# Revit family: Flush_valve-Manual-Zurn-Exposed-Water_closet-Z6000
name_source: partatom
category: Plumbing Fixtures
units: mm (PartAtom-declared; Revit-internal decimal feet)

## family parameters
Cut with Voids When Loaded = No
Host = Face
Maintain Annotation Orientation = No
OmniClass Number = 23.45.05.14.99
OmniClass Title = Other Sanitary Washing Plumbing Fixtures
Part Type = Normal
Room Calculation Point = No
Round Connector Dimension = Use Radius
Shared = No

## types (24) — shared parameters
Activation Method = Manual Operated
Assembly Code = D2010.60
CW Connection = Yes
Centerline of Stop Valve to Centerline of Flush Valve = 4.75 "
Default Elevation = 48 "
Description = Exposed Flush Valve for Water Closets
HW Connection = No
Inlet Connection Size (inch) = 1 "
Main Material = Chrome-Plated Brass - Zurn - Polished
Manufacturer = Zurn Water, LLC
Manufacturer Brand = Zurn
Max Working Water Temperature = 104 °F
Model = Z6000
Modified Date = 07/31/2025
Operating Water Pressure (PSI) = 25 – 80 PSI (172 – 552 kPa)
Product Documentation Link = https://files.zurn.com
Product Installation Sheet URL = https://files.zurn.com
Product Page URL = https://www.zurn.com
Product data URL = https://www.bimobject.com
Repair Parts URL = https://files.zurn.com
URL = https://www.zurn.com
Vent Connection = No
Waste Connection = No
zero-valued in all types: CWFU, HWFU, WFU

## per-type parameters (varying)
| type | Flush Rate (GPF) | Type Comments |
| Z6000-ONE (1.1 GPF, 11-1/2") | 1.1 GPF | Z6000-ONE (1.1 GPF, 11-1/2" R-I) |
| Z6000-HET (1.28 GPF, 11-1/2") | 1.28 GPF | Z6000-HET (1.28 GPF, 11-1/2" R-I) |
| Z6000-WS1-DF (1.6 GPF / 1.1 GPF, 11-1/2") | 1.6 GPF / 1.1 GPF | Z6000-WS1-DF (1.6 GPF / 1.1 GPF, 11-1/2" R-I) |
| Z6000-DF (3.5 GPF / 2.4 GPF, 11-1/2") | 3.5 GPF / 2.4 GPF | Z6000-DF (3.5 GPF / 2.4 GPF, 11-1/2" R-I) |
| Z6000-WS1 (1.6 GPF, 11-1/2") | 1.6 GPF | Z6000-WS1 (1.6 GPF, 11-1/2" R-I) |
| Z6000 (3.5 GPF, 11-1/2") | 3.5 GPF | Z6000 (3.5 GPF, 11-1/2" R-I) |
| Z6000-1-ONE (1.1 GPF, 16") | 1.1 GPF | Z6000-1-ONE (1.1 GPF, 16" R-I) |
| Z6000-1-HET (1.28 GPF, 16") | 1.28 GPF | Z6000-1-HET (1.28 GPF, 16" R-I) |
| Z6000-1-WS1-DF (1.6 GPF / 1.1 GPF, 16") | 1.6 GPF / 1.1 GPF | Z6000-1-WS1-DF (1.6 GPF / 1.1 GPF, 16" R-I) |
| Z6000-1-DF (3.5 GPF / 2.4 GPF, 16") | 3.5 GPF / 2.4 GPF | Z6000-1-DF (3.5 GPF / 2.4 GPF, 16" R-I) |
| Z6000-1-WS1 (1.6 GPF, 16") | 1.6 GPF | Z6000-1-WS1 (1.6 GPF, 16" R-I) |
| Z6000-1 (3.5 GPF, 16") | 3.5 GPF | Z6000-1 (3.5 GPF, 16" R-I) |
| Z6000-2-ONE (1.1 GPF, 24") | 1.1 GPF | Z6000-2-ONE (1.1 GPF, 24" R-I) |
| Z6000-2-HET (1.28 GPF, 24") | 1.28 GPF | Z6000-2-HET (1.28 GPF, 24" R-I) |
| Z6000-2-WS1-DF (1.6 GPF / 1.1 GPF, 24") | 1.6 GPF / 1.1 GPF | Z6000-2-WS1-DF (1.6 GPF / 1.1 GPF, 24" R-I) |
| Z6000-2-DF (3.5 GPF / 2.4 GPF, 24") | 3.5 GPF / 2.4 GPF | Z6000-2-DF (3.5 GPF / 2.4 GPF, 24" R-I) |
| Z6000-2-WS1 (1.6 GPF, 24") | 1.6 GPF | Z6000-2-WS1 (1.6 GPF, 24" R-I) |
| Z6000-2 (3.5 GPF, 24") | 3.5 GPF | Z6000-2 (3.5 GPF, 24" R-I) |
| Z6000-3-ONE (1.1 GPF, 27") | 1.1 GPF | Z6000-3-ONE (1.1 GPF, 27" R-I) |
| Z6000-3-HET (1.28 GPF, 27") | 1.28 GPF | Z6000-3-HET (1.28 GPF, 27" R-I) |
| Z6000-3-WS1-DF (1.6 GPF / 1.1 GPF, 27") | 1.6 GPF / 1.1 GPF | Z6000-3-WS1-DF (1.6 GPF / 1.1 GPF, 27" R-I) |
| Z6000-3-DF (3.5 GPF / 2.4 GPF, 27") | 3.5 GPF / 2.4 GPF | Z6000-3-DF (3.5 GPF / 2.4 GPF, 27" R-I) |
| Z6000-3-WS1 (1.6 GPF, 27") | 1.6 GPF | Z6000-3-WS1 (1.6 GPF, 27" R-I) |
| Z6000-3 (3.5 GPF, 27") | 3.5 GPF | Z6000-3 (3.5 GPF, 27" R-I) |

## geometry (parser evidence)
native form markers: Blend x8, Sweep x14
no freeform markers — native parametric forms only
